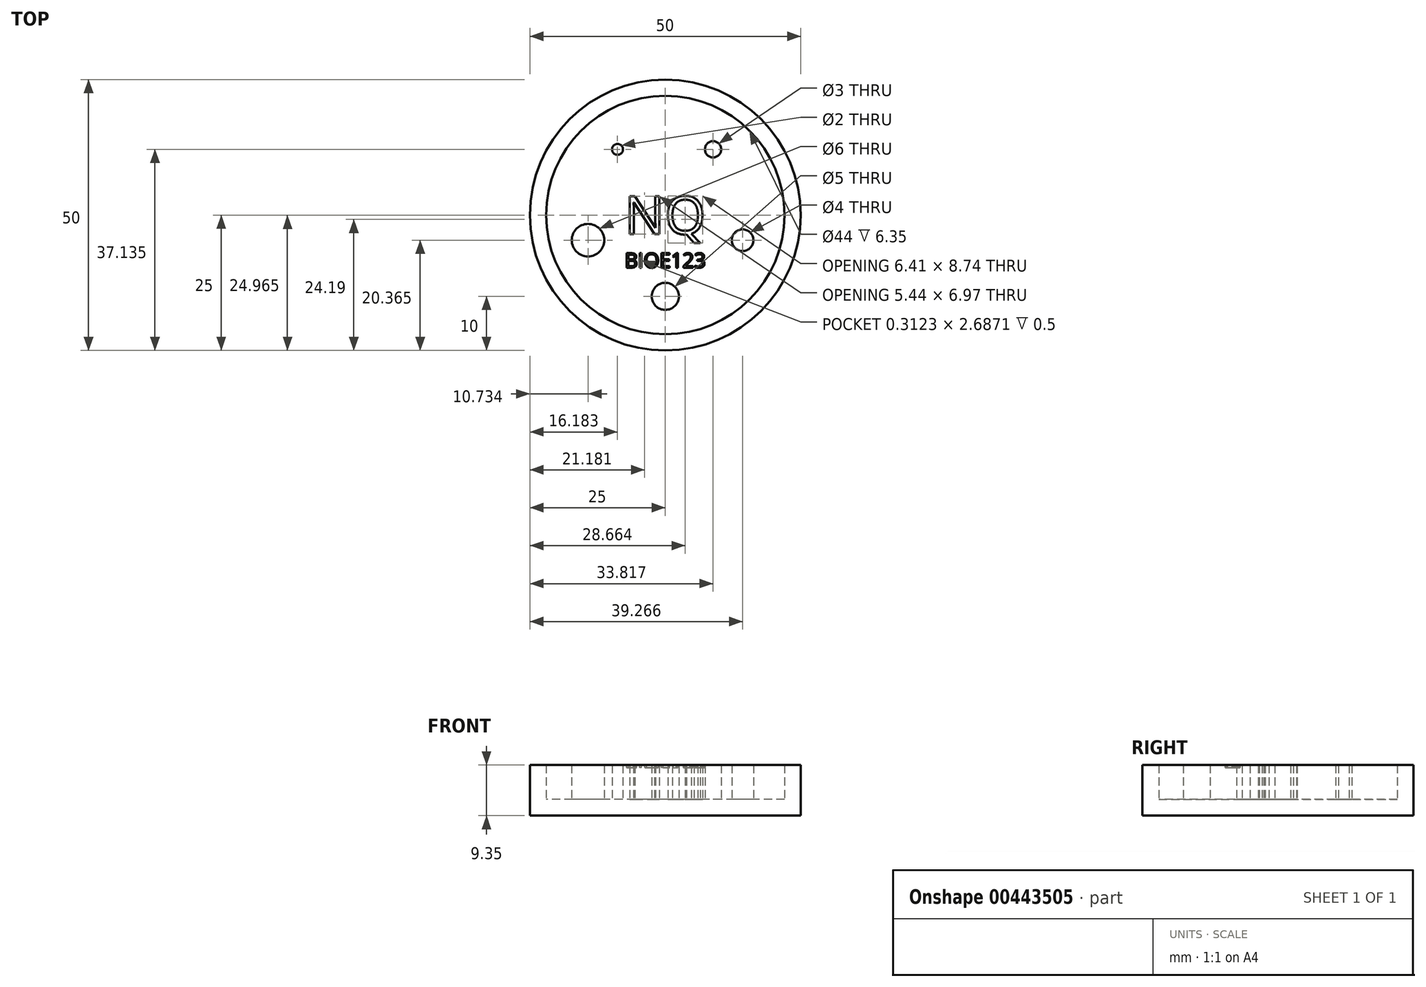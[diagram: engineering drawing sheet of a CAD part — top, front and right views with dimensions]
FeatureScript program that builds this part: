
annotation { "Feature Type Name" : "Feature", "Feature Type Description" : "" }
export const myFeature = defineFeature(function(context is Context, id is Id, definition is map)
    precondition{}
    {
        {
            var Q0;
            Q0=qCreatedBy(makeId("Top.planeOp"),FACE);
            var sketch = newSketch(context, id + "F0", { "sketchPlane" : qUnion([Q0])});
            skCircle(sketch, "E0", {"center": v(0, 0) * mm, "radius": 25 * mm});
            skSolve(sketch);
        }
        {
            var Q0;
            Q0=makeQuery(id+"F0.imprint","IMPRINT",FACE,{"disambiguationData":[TD([[makeQuery(id+"F0.imprint","IMPRINT",EDGE,{"derivedFrom":sQuery(id+"F0.wireOp",EDGE,"E0")}),1.0]])]});
            extrude(context, id + "F1", {"entities" : qUnion([Q0]), "depth" : 3 * mm});
        }
        {
            var Q0;
            Q0=makeQuery(id+"F1.opExtrude","CAP_FACE",FACE,{"disambiguationData":[OSD([sQuery(id+"F0.wireOp",EDGE,"E0")])],"isStart":false});
            var sketch = newSketch(context, id + "F2", { "sketchPlane" : qUnion([Q0])});
            skCircle(sketch, "E1", {"center": v(0, 0) * mm, "radius": 22 * mm});
            skCircle(sketch, "E2", {"center": v(-8.82, 12.14) * mm, "radius": 1 * mm});
            skCircle(sketch, "E3", {"center": v(8.82, 12.14) * mm, "radius": 1.5 * mm});
            skCircle(sketch, "E4", {"center": v(-14.27, -4.64) * mm, "radius": 3 * mm});
            skCircle(sketch, "E5", {"center": v(0, 0) * mm, "radius": 15 * mm});
            skCircle(sketch, "E6", {"center": v(14.27, -4.64) * mm, "radius": 2 * mm});
            skCircle(sketch, "E7", {"center": v(0, -15) * mm, "radius": 2.5 * mm});
            skLineSegment(sketch, "E8", {"start": v(-8.82, 12.14) * mm, "end": v(8.82, 12.14) * mm, "construction": true});
            skLineSegment(sketch, "E9", {"start": v(8.82, 12.14) * mm, "end": v(14.27, -4.64) * mm, "construction": true});
            skLineSegment(sketch, "E10", {"start": v(14.27, -4.64) * mm, "end": v(0, -15) * mm, "construction": true});
            skLineSegment(sketch, "E11", {"start": v(0, -15) * mm, "end": v(-14.27, -4.64) * mm, "construction": true});
            skLineSegment(sketch, "E12", {"start": v(-14.27, -4.64) * mm, "end": v(-8.82, 12.14) * mm, "construction": true});
            skLineSegment(sketch, "E13", {"start": v(0, 0) * mm, "end": v(0, -25) * mm, "construction": true});
            skText(sketch, "E14", { "text": "NQ", "fontName": "OpenSans-Regular.ttf"});
            const initialGuessF2  = {"E14": [-0.0075, -0.00352, 1, 0, 0.00703]};
            skSetInitialGuess(sketch, initialGuessF2);
            skSolve(sketch);
        }
        {
            var Q0;
            Q0=makeQuery(id+"F2.imprint","IMPRINT",FACE,{"disambiguationData":[TD([[makeQuery(id+"F2.imprint","IMPRINT",EDGE,{"derivedFrom":sQuery(id+"F2.wireOp",EDGE,"E1")}),-1.0]])]});
            var Q1;
            {var subQ0=sQuery(id+"F2.wireOp",EDGE,"E5");var subQ1=sQuery(id+"F2.wireOp",EDGE,"E2");var subQ2=makeQuery(id+"F2.imprint","INTERSECT",VERTEX,{"disambiguationData":[OD(0.0)],"derivedFrom":[subQ1,subQ0]});Q1=makeQuery(id+"F2.imprint","IMPRINT",FACE,{"disambiguationData":[TD([[makeQuery(id+"F2.imprint","IMPRINT",EDGE,{"disambiguationData":[TD([[subQ2,-1.0]])],"derivedFrom":subQ1}),1.0]])]});}
            var Q2;
            {var subQ0=sQuery(id+"F2.wireOp",EDGE,"E5");var subQ1=sQuery(id+"F2.wireOp",EDGE,"E2");var subQ2=makeQuery(id+"F2.imprint","INTERSECT",VERTEX,{"disambiguationData":[OD(0.0)],"derivedFrom":[subQ1,subQ0]});Q2=makeQuery(id+"F2.imprint","IMPRINT",FACE,{"disambiguationData":[TD([[makeQuery(id+"F2.imprint","IMPRINT",EDGE,{"disambiguationData":[TD([[subQ2,1.0]])],"derivedFrom":subQ1}),1.0]])]});}
            var Q3;
            {var subQ0=sQuery(id+"F2.wireOp",EDGE,"E5");var subQ1=sQuery(id+"F2.wireOp",EDGE,"E3");var subQ2=makeQuery(id+"F2.imprint","INTERSECT",VERTEX,{"disambiguationData":[OD(0.0)],"derivedFrom":[subQ1,subQ0]});Q3=makeQuery(id+"F2.imprint","IMPRINT",FACE,{"disambiguationData":[TD([[makeQuery(id+"F2.imprint","IMPRINT",EDGE,{"disambiguationData":[TD([[subQ2,-1.0]])],"derivedFrom":subQ1}),1.0]])]});}
            var Q4;
            {var subQ0=sQuery(id+"F2.wireOp",EDGE,"E5");var subQ1=sQuery(id+"F2.wireOp",EDGE,"E3");var subQ2=makeQuery(id+"F2.imprint","INTERSECT",VERTEX,{"disambiguationData":[OD(0.0)],"derivedFrom":[subQ1,subQ0]});Q4=makeQuery(id+"F2.imprint","IMPRINT",FACE,{"disambiguationData":[TD([[makeQuery(id+"F2.imprint","IMPRINT",EDGE,{"disambiguationData":[TD([[subQ2,1.0]])],"derivedFrom":subQ1}),1.0]])]});}
            var Q5;
            {var subQ0=sQuery(id+"F2.wireOp",EDGE,"E6");var subQ1=sQuery(id+"F2.wireOp",EDGE,"E5");var subQ2=makeQuery(id+"F2.imprint","INTERSECT",VERTEX,{"disambiguationData":[OD(0.0)],"derivedFrom":[subQ1,subQ0]});Q5=makeQuery(id+"F2.imprint","IMPRINT",FACE,{"disambiguationData":[TD([[makeQuery(id+"F2.imprint","IMPRINT",EDGE,{"disambiguationData":[TD([[subQ2,-1.0]])],"derivedFrom":subQ1}),1.0]])]});}
            var Q6;
            {var subQ0=sQuery(id+"F2.wireOp",EDGE,"E6");var subQ1=sQuery(id+"F2.wireOp",EDGE,"E5");var subQ2=makeQuery(id+"F2.imprint","INTERSECT",VERTEX,{"disambiguationData":[OD(0.0)],"derivedFrom":[subQ1,subQ0]});Q6=makeQuery(id+"F2.imprint","IMPRINT",FACE,{"disambiguationData":[TD([[makeQuery(id+"F2.imprint","IMPRINT",EDGE,{"disambiguationData":[TD([[subQ2,-1.0]])],"derivedFrom":subQ1}),-1.0]])]});}
            var Q7;
            {var subQ0=sQuery(id+"F2.wireOp",EDGE,"E7");var subQ1=sQuery(id+"F2.wireOp",EDGE,"E5");var subQ2=makeQuery(id+"F2.imprint","INTERSECT",VERTEX,{"disambiguationData":[OD(0.0)],"derivedFrom":[subQ1,subQ0]});Q7=makeQuery(id+"F2.imprint","IMPRINT",FACE,{"disambiguationData":[TD([[makeQuery(id+"F2.imprint","IMPRINT",EDGE,{"disambiguationData":[TD([[subQ2,-1.0]])],"derivedFrom":subQ1}),1.0]])]});}
            var Q8;
            {var subQ0=sQuery(id+"F2.wireOp",EDGE,"E7");var subQ1=sQuery(id+"F2.wireOp",EDGE,"E5");var subQ2=makeQuery(id+"F2.imprint","INTERSECT",VERTEX,{"disambiguationData":[OD(0.0)],"derivedFrom":[subQ1,subQ0]});Q8=makeQuery(id+"F2.imprint","IMPRINT",FACE,{"disambiguationData":[TD([[makeQuery(id+"F2.imprint","IMPRINT",EDGE,{"disambiguationData":[TD([[subQ2,-1.0]])],"derivedFrom":subQ1}),-1.0]])]});}
            var Q9;
            {var subQ0=sQuery(id+"F2.wireOp",EDGE,"E5");var subQ1=sQuery(id+"F2.wireOp",EDGE,"E4");var subQ2=makeQuery(id+"F2.imprint","INTERSECT",VERTEX,{"disambiguationData":[OD(0.0)],"derivedFrom":[subQ1,subQ0]});Q9=makeQuery(id+"F2.imprint","IMPRINT",FACE,{"disambiguationData":[TD([[makeQuery(id+"F2.imprint","IMPRINT",EDGE,{"disambiguationData":[TD([[subQ2,-1.0]])],"derivedFrom":subQ1}),1.0]])]});}
            var Q10;
            {var subQ0=sQuery(id+"F2.wireOp",EDGE,"E5");var subQ1=sQuery(id+"F2.wireOp",EDGE,"E4");var subQ2=makeQuery(id+"F2.imprint","INTERSECT",VERTEX,{"disambiguationData":[OD(0.0)],"derivedFrom":[subQ1,subQ0]});Q10=makeQuery(id+"F2.imprint","IMPRINT",FACE,{"disambiguationData":[TD([[makeQuery(id+"F2.imprint","IMPRINT",EDGE,{"disambiguationData":[TD([[subQ2,1.0]])],"derivedFrom":subQ1}),1.0]])]});}
            var Q11;
            Q11=makeQuery(id+"F2.imprint","IMPRINT",FACE,{"disambiguationData":[TD([[makeQuery(id+"F2.imprint","IMPRINT",EDGE,{"derivedFrom":sQuery(id+"F2.wireOp",EDGE,"E14.sketch_text.stroke-0")}),-1.0]])]});
            var Q12;
            Q12=makeQuery(id+"F2.imprint","IMPRINT",FACE,{"disambiguationData":[TD([[makeQuery(id+"F2.imprint","IMPRINT",EDGE,{"derivedFrom":sQuery(id+"F2.wireOp",EDGE,"E14.sketch_text.stroke-15")}),-1.0]])]});
            extrude(context, id + "F3", {"entities" : qUnion([Q0, Q1, Q2, Q3, Q4, Q5, Q6, Q7, Q8, Q9, Q10, Q11, Q12]), "operationType" : NewBodyOperationType.ADD, "depth" : 6.35 * mm});
        }
        {
            var Q0;
            Q0=makeQuery(id+"F2.imprint","IMPRINT",FACE,{"disambiguationData":[TD([[makeQuery(id+"F2.imprint","IMPRINT",EDGE,{"derivedFrom":sQuery(id+"F2.wireOp",EDGE,"E1")}),1.0]])]});
            var Q1;
            Q1=makeQuery(id+"F2.imprint","IMPRINT",FACE,{"disambiguationData":[TD([[makeQuery(id+"F2.imprint","IMPRINT",EDGE,{"derivedFrom":sQuery(id+"F2.wireOp",EDGE,"E14.sketch_text.stroke-0")}),1.0]])]});
            var Q2;
            Q2=makeQuery(id+"F1.opExtrude","SWEPT_BODY",BODY,{"disambiguationData":[OSD([sQuery(id+"F0.wireOp",EDGE,"E0")])]});
            extrude(context, id + "F4", {"entities" : qUnion([Q0, Q1]), "endBoundEntityBody" : qUnion([Q2]), "depth" : 6.35 * mm});
        }
        {
            var Q0;
            Q0=makeQuery(id+"F4.opExtrude","CAP_FACE",FACE,{"disambiguationData":[OSD([sQuery(id+"F2.wireOp",EDGE,"E1"),sQuery(id+"F2.wireOp",EDGE,"E2"),sQuery(id+"F2.wireOp",EDGE,"E3"),sQuery(id+"F2.wireOp",EDGE,"E4"),sQuery(id+"F2.wireOp",EDGE,"E6"),sQuery(id+"F2.wireOp",EDGE,"E7"),sQuery(id+"F2.wireOp",EDGE,"E14.sketch_text.stroke-0"),sQuery(id+"F2.wireOp",EDGE,"E14.sketch_text.stroke-1"),sQuery(id+"F2.wireOp",EDGE,"E14.sketch_text.stroke-2"),sQuery(id+"F2.wireOp",EDGE,"E14.sketch_text.stroke-3"),sQuery(id+"F2.wireOp",EDGE,"E14.sketch_text.stroke-4"),sQuery(id+"F2.wireOp",EDGE,"E14.sketch_text.stroke-5"),sQuery(id+"F2.wireOp",EDGE,"E14.sketch_text.stroke-6"),sQuery(id+"F2.wireOp",EDGE,"E14.sketch_text.stroke-7"),sQuery(id+"F2.wireOp",EDGE,"E14.sketch_text.stroke-8"),sQuery(id+"F2.wireOp",EDGE,"E14.sketch_text.stroke-9"),sQuery(id+"F2.wireOp",EDGE,"E14.sketch_text.stroke-10"),sQuery(id+"F2.wireOp",EDGE,"E14.sketch_text.stroke-11"),sQuery(id+"F2.wireOp",EDGE,"E14.sketch_text.stroke-12"),sQuery(id+"F2.wireOp",EDGE,"E14.sketch_text.stroke-13"),sQuery(id+"F2.wireOp",EDGE,"E14.sketch_text.stroke-14"),sQuery(id+"F2.wireOp",EDGE,"E14.sketch_text.stroke-15"),sQuery(id+"F2.wireOp",EDGE,"E14.sketch_text.stroke-16"),sQuery(id+"F2.wireOp",EDGE,"E14.sketch_text.stroke-17"),sQuery(id+"F2.wireOp",EDGE,"E14.sketch_text.stroke-18"),sQuery(id+"F2.wireOp",EDGE,"E14.sketch_text.stroke-19"),sQuery(id+"F2.wireOp",EDGE,"E14.sketch_text.stroke-20"),sQuery(id+"F2.wireOp",EDGE,"E14.sketch_text.stroke-21"),sQuery(id+"F2.wireOp",EDGE,"E14.sketch_text.stroke-22"),sQuery(id+"F2.wireOp",EDGE,"E14.sketch_text.stroke-23"),sQuery(id+"F2.wireOp",EDGE,"E14.sketch_text.stroke-24"),sQuery(id+"F2.wireOp",EDGE,"E14.sketch_text.stroke-25"),sQuery(id+"F2.wireOp",EDGE,"E14.sketch_text.stroke-26")])],"isStart":false});
            var sketch = newSketch(context, id + "F5", { "sketchPlane" : qUnion([Q0])});
            skText(sketch, "E15", { "text": "BIOE123", "fontName": "OpenSans-Regular.ttf"});
            const initialGuessF5  = {"E15": [-0.0075, -0.00971, 1, 0, 0.00271]};
            skSetInitialGuess(sketch, initialGuessF5);
            skSolve(sketch);
        }
        {
            var Q0;
            Q0 = qSketchRegion(id + "F5", true);
            extrude(context, id + "F6", {"entities" : qUnion([Q0]), "operationType" : NewBodyOperationType.REMOVE, "oppositeDirection" : true, "depth" : 0.5 * mm});
        }
    });
